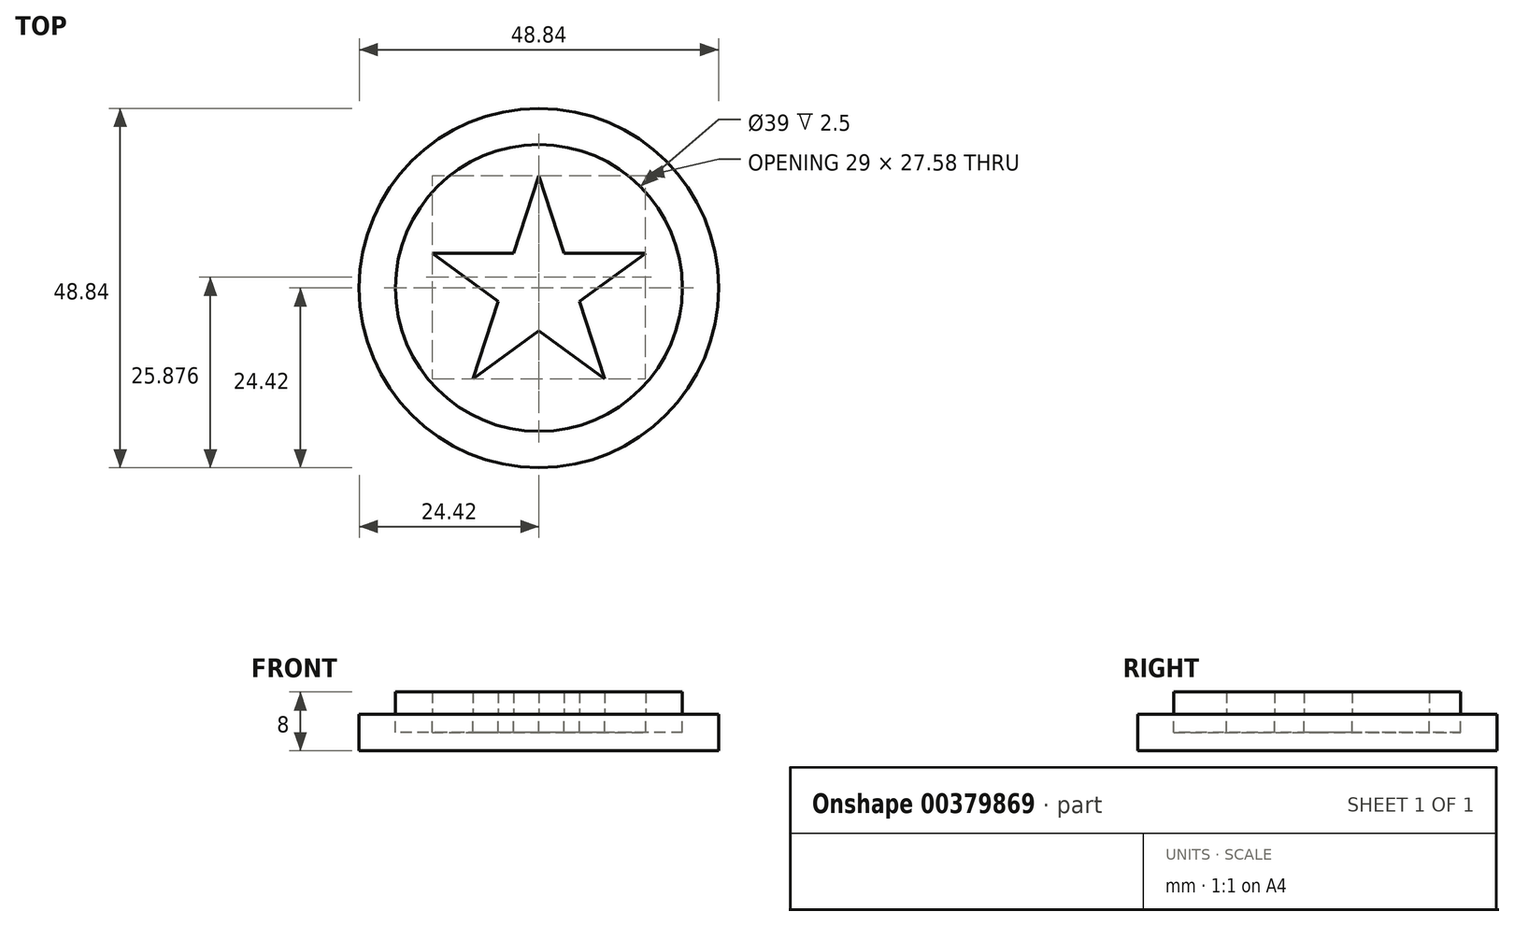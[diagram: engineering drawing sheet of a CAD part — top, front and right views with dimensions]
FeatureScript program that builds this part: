
annotation { "Feature Type Name" : "Feature", "Feature Type Description" : "" }
export const myFeature = defineFeature(function(context is Context, id is Id, definition is map)
    precondition{}
    {
        {
            var Q0;
            Q0=qCreatedBy(makeId("Top.planeOp"),FACE);
            var sketch = newSketch(context, id + "F0", { "sketchPlane" : qUnion([Q0])});
            skLineSegment(sketch, "E0", {"start": v(-8.96, -12.33) * mm, "end": v(0, 15.25) * mm});
            skLineSegment(sketch, "E1", {"start": v(0, 15.25) * mm, "end": v(8.96, -12.33) * mm});
            skLineSegment(sketch, "E2", {"start": v(8.96, -12.33) * mm, "end": v(-14.5, 4.71) * mm});
            skLineSegment(sketch, "E3", {"start": v(-14.5, 4.71) * mm, "end": v(14.5, 4.71) * mm});
            skLineSegment(sketch, "E4", {"start": v(14.5, 4.71) * mm, "end": v(-8.96, -12.33) * mm});
            skLineSegment(sketch, "E5", {"start": v(0, -5.82) * mm, "end": v(0, 4.71) * mm, "construction": true});
            skCircle(sketch, "E6", {"center": v(0, 0) * mm, "radius": 19.5 * mm});
            skLineSegment(sketch, "E7", {"start": v(5.54, -1.8) * mm, "end": v(-4.48, 1.46) * mm, "construction": true});
            skLineSegment(sketch, "E8", {"start": v(3.42, 4.71) * mm, "end": v(-2.77, -3.81) * mm, "construction": true});
            skLineSegment(sketch, "E9", {"start": v(-3.42, 4.71) * mm, "end": v(2.77, -3.81) * mm, "construction": true});
            skLineSegment(sketch, "E10", {"start": v(-5.54, -1.8) * mm, "end": v(4.48, 1.46) * mm, "construction": true});
            skSolve(sketch);
        }
        {
            var Q0;
            Q0=makeQuery(id+"F0.imprint","IMPRINT",FACE,{"disambiguationData":[TD([[makeQuery(id+"F0.imprint","IMPRINT",EDGE,{"derivedFrom":sQuery(id+"F0.wireOp",EDGE,"E6")}),1.0]])]});
            extrude(context, id + "F1", {"entities" : qUnion([Q0]), "depth" : 3 * mm});
        }
        {
            var Q0;
            Q0=makeQuery(id+"F1.opExtrude","CAP_FACE",FACE,{"disambiguationData":[OSD([sQuery(id+"F0.wireOp",EDGE,"E0"),sQuery(id+"F0.wireOp",EDGE,"E1"),sQuery(id+"F0.wireOp",EDGE,"E2"),sQuery(id+"F0.wireOp",EDGE,"E3"),sQuery(id+"F0.wireOp",EDGE,"E4"),sQuery(id+"F0.wireOp",EDGE,"E6")])],"isStart":true});
            var sketch = newSketch(context, id + "F2", { "sketchPlane" : qUnion([Q0])});
            skCircle(sketch, "E11", {"center": v(0, 0) * mm, "radius": 24.42 * mm});
            skSolve(sketch);
        }
        {
            var Q0;
            Q0 = qSketchRegion(id + "F2", true);
            extrude(context, id + "F3", {"entities" : qUnion([Q0]), "depth" : 5 * mm});
        }
        {
            var Q0;
            Q0=makeQuery(id+"F1.opExtrude","CAP_FACE",FACE,{"disambiguationData":[OSD([sQuery(id+"F0.wireOp",EDGE,"E0"),sQuery(id+"F0.wireOp",EDGE,"E1"),sQuery(id+"F0.wireOp",EDGE,"E2"),sQuery(id+"F0.wireOp",EDGE,"E3"),sQuery(id+"F0.wireOp",EDGE,"E4"),sQuery(id+"F0.wireOp",EDGE,"E6")])],"isStart":true});
            extrude(context, id + "F4", {"entities" : qUnion([Q0]), "operationType" : NewBodyOperationType.REMOVE, "depth" : 2.5 * mm});
        }
    });
